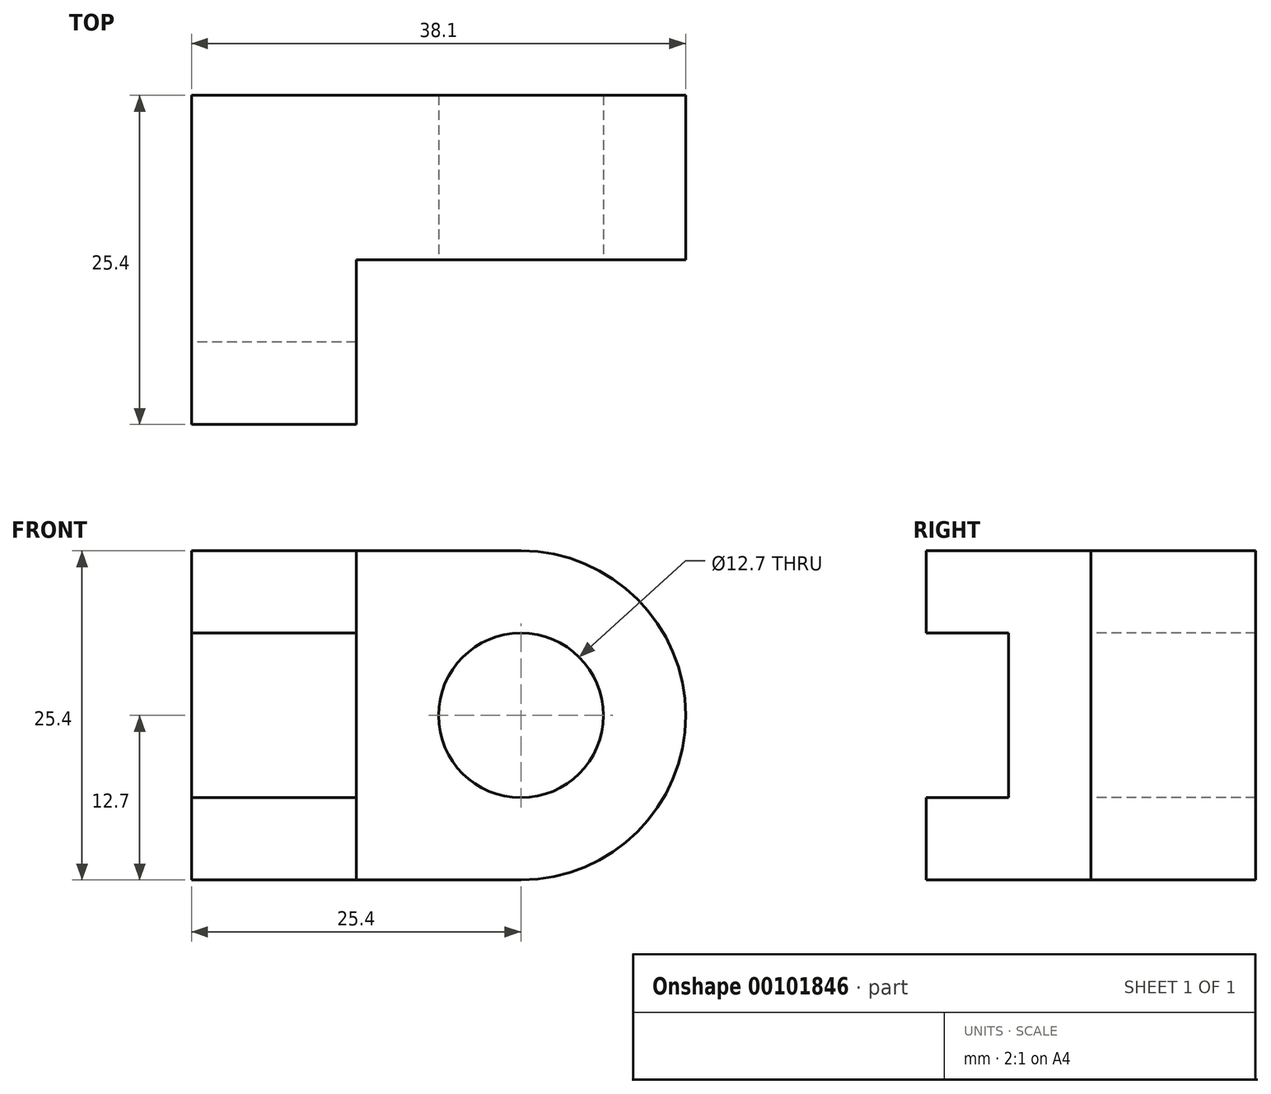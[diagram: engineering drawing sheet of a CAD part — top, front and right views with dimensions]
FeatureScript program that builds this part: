
annotation { "Feature Type Name" : "Feature", "Feature Type Description" : "" }
export const myFeature = defineFeature(function(context is Context, id is Id, definition is map)
    precondition{}
    {
        {
            var Q0;
            Q0=qCreatedBy(makeId("Top.planeOp"),FACE);
            var sketch = newSketch(context, id + "F0", { "sketchPlane" : qUnion([Q0])});
            skLineSegment(sketch, "E0", {"start": v(0, 0) * mm, "end": v(38.1, 0) * mm});
            skLineSegment(sketch, "E1", {"start": v(38.1, 0) * mm, "end": v(38.1, -12.7) * mm});
            skLineSegment(sketch, "E2", {"start": v(38.1, -12.7) * mm, "end": v(12.7, -12.7) * mm});
            skLineSegment(sketch, "E3", {"start": v(12.7, -12.7) * mm, "end": v(12.7, -25.4) * mm});
            skLineSegment(sketch, "E4", {"start": v(12.7, -25.4) * mm, "end": v(0, -25.4) * mm});
            skLineSegment(sketch, "E5", {"start": v(0, -25.4) * mm, "end": v(0, 0) * mm});
            skSolve(sketch);
        }
        {
            var Q0;
            Q0 = qSketchRegion(id + "F0", true);
            extrude(context, id + "F1", {"entities" : qUnion([Q0]), "depth" : 25.4 * mm});
        }
        {
            var Q0;
            Q0=makeQuery(id+"F1.opExtrude","SWEPT_FACE",FACE,{"disambiguationData":[OSD([sQuery(id+"F0.wireOp",EDGE,"E2")])]});
            var sketch = newSketch(context, id + "F2", { "sketchPlane" : qUnion([Q0])});
            skLineSegment(sketch, "E6", {"start": v(12.7, 12.7) * mm, "end": v(38.1, 12.7) * mm, "construction": true});
            skLineSegment(sketch, "E7", {"start": v(25.4, 25.4) * mm, "end": v(25.4, 0) * mm, "construction": true});
            skCircle(sketch, "E8", {"center": v(25.4, 12.7) * mm, "radius": 6.35 * mm});
            skSolve(sketch);
        }
        {
            var Q0;
            Q0=makeQuery(id+"F2.imprint","IMPRINT",FACE,{"disambiguationData":[TD([[makeQuery(id+"F2.imprint","IMPRINT",EDGE,{"derivedFrom":sQuery(id+"F2.wireOp",EDGE,"E8")}),1.0]])]});
            extrude(context, id + "F3", {"entities" : qUnion([Q0]), "operationType" : NewBodyOperationType.REMOVE, "endBound" : BoundingType.THROUGH_ALL, "oppositeDirection" : true, "depth" : 25.4 * mm});
        }
        {
            var Q0;
            Q0=makeQuery(id+"F1.opExtrude","SWEPT_FACE",FACE,{"disambiguationData":[OSD([sQuery(id+"F0.wireOp",EDGE,"E0")])]});
            var sketch = newSketch(context, id + "F4", { "sketchPlane" : qUnion([Q0])});
            skArc(sketch, "E9", {"start": v(-25.4, 25.4) * mm, "mid": v(-38.1, 12.7) * mm, "end": v(-25.4, 0) * mm});
            skSolve(sketch);
        }
        {
            var Q0;
            {var subQ0=sQuery(id+"F4.wireOp",EDGE,"E9");var subQ1=sQuery(id+"F0.wireOp",EDGE,"E0");var subQ2=makeQuery(id+"F1.opExtrude","CAP_EDGE",EDGE,{"disambiguationData":[OSD([subQ1])],"isStart":true});var subQ3=makeQuery(id+"F4.imprint","INTERSECT",VERTEX,{"derivedFrom":[subQ2,subQ0]});Q0=makeQuery(id+"F4.imprint","IMPRINT",FACE,{"disambiguationData":[TD([[makeQuery(id+"F4.imprint","IMPRINT",EDGE,{"disambiguationData":[TD([[subQ3,1.0]])],"derivedFrom":subQ0}),-1.0]])]});}
            var Q1;
            {var subQ0=sQuery(id+"F4.wireOp",EDGE,"E9");var subQ1=sQuery(id+"F0.wireOp",EDGE,"E0");var subQ2=makeQuery(id+"F1.opExtrude","CAP_EDGE",EDGE,{"disambiguationData":[OSD([subQ1])],"isStart":false});var subQ3=makeQuery(id+"F4.imprint","INTERSECT",VERTEX,{"derivedFrom":[subQ2,subQ0]});Q1=makeQuery(id+"F4.imprint","IMPRINT",FACE,{"disambiguationData":[TD([[makeQuery(id+"F4.imprint","IMPRINT",EDGE,{"disambiguationData":[TD([[subQ3,-1.0]])],"derivedFrom":subQ0}),-1.0]])]});}
            extrude(context, id + "F5", {"entities" : qUnion([Q0, Q1]), "operationType" : NewBodyOperationType.REMOVE, "endBound" : BoundingType.THROUGH_ALL, "oppositeDirection" : true, "depth" : 12.7 * mm});
        }
        {
            var Q0;
            Q0=makeQuery(id+"F1.opExtrude","SWEPT_FACE",FACE,{"disambiguationData":[OSD([sQuery(id+"F0.wireOp",EDGE,"E5")])]});
            var sketch = newSketch(context, id + "F6", { "sketchPlane" : qUnion([Q0])});
            skLineSegment(sketch, "E10.bottom", {"start": v(25.4, 19.05) * mm, "end": v(19.05, 19.05) * mm});
            skLineSegment(sketch, "E10.top", {"start": v(25.4, 6.35) * mm, "end": v(19.05, 6.35) * mm});
            skLineSegment(sketch, "E10.left", {"start": v(25.4, 19.05) * mm, "end": v(25.4, 6.35) * mm});
            skLineSegment(sketch, "E10.right", {"start": v(19.05, 19.05) * mm, "end": v(19.05, 6.35) * mm});
            skSolve(sketch);
        }
        {
            var Q0;
            Q0 = qSketchRegion(id + "F6", true);
            extrude(context, id + "F7", {"entities" : qUnion([Q0]), "operationType" : NewBodyOperationType.REMOVE, "endBound" : BoundingType.THROUGH_ALL, "oppositeDirection" : true, "depth" : 25.4 * mm});
        }
    });
